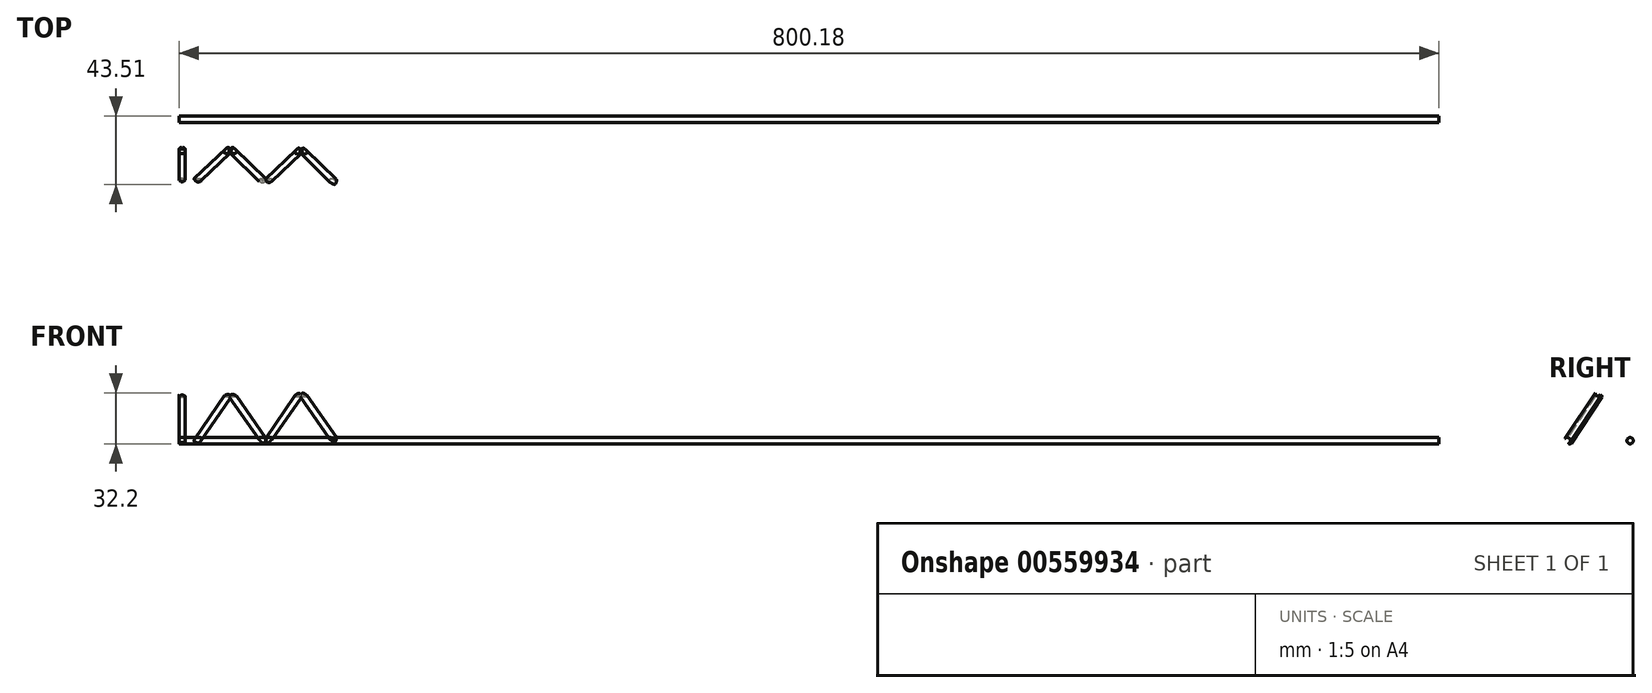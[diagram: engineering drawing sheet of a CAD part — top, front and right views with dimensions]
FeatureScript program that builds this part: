
annotation { "Feature Type Name" : "Feature", "Feature Type Description" : "" }
export const myFeature = defineFeature(function(context is Context, id is Id, definition is map)
    precondition{}
    {
        {
            var Q0;
            Q0=qCreatedBy(makeId("Front.planeOp"),FACE);
            var sketch = newSketch(context, id + "F0", { "sketchPlane" : qUnion([Q0])});
            skLineSegment(sketch, "E0", {"start": v(0, 0) * mm, "end": v(-100, 0) * mm, "construction": true});
            skLineSegment(sketch, "E1", {"start": v(0, 0) * mm, "end": v(700, 0) * mm, "construction": true});
            skLineSegment(sketch, "E2", {"start": v(0, 0) * mm, "end": v(0, 30) * mm, "construction": true});
            skLineSegment(sketch, "E3", {"start": v(0, 30) * mm, "end": v(700, 30) * mm});
            skLineSegment(sketch, "E4", {"start": v(700, 28) * mm, "end": v(700, 30) * mm});
            skLineSegment(sketch, "E5", {"start": v(700, 28) * mm, "end": v(-100, 28) * mm});
            skLineSegment(sketch, "E6", {"start": v(-100, 30) * mm, "end": v(-100, 28) * mm});
            skLineSegment(sketch, "E7", {"start": v(-100, 30) * mm, "end": v(0, 30) * mm});
            skPoint(sketch, "E8", {"position": v(0, 30) * mm});
            skSolve(sketch);
        }
        {
            var Q0;
            Q0=makeQuery(id+"F0.imprint","IMPRINT",FACE,{"disambiguationData":[TD([[makeQuery(id+"F0.imprint","IMPRINT",EDGE,{"derivedFrom":sQuery(id+"F0.wireOp",EDGE,"E3")}),-1.0]])]});
            var Q1;
            Q1=sQuery(id+"F0.wireOp",EDGE,"E7");
            revolve(context, id + "F1", {"surfaceOperationType" : NewSurfaceOperationType.NEW, "entities" : qUnion([Q0]), "axis" : qUnion([Q1]), "revolveType" : RevolveType.FULL});
        }
        {
            var Q0;
            Q0=qCreatedBy(makeId("Right.planeOp"),FACE);
            var sketch = newSketch(context, id + "F2", { "sketchPlane" : qUnion([Q0])});
            skLineSegment(sketch, "E9", {"start": v(0, 0) * mm, "end": v(-20, 0) * mm, "construction": true});
            skLineSegment(sketch, "E10", {"start": v(0, 0) * mm, "end": v(20, 0) * mm, "construction": true});
            skCircle(sketch, "E11", {"center": v(-20, 0) * mm, "radius": 2 * mm});
            skCircle(sketch, "E12", {"center": v(20, 0) * mm, "radius": 2 * mm});
            skSolve(sketch);
        }
        {
            var Q0;
            Q0=makeQuery(id+"F2.imprint","IMPRINT",FACE,{"disambiguationData":[TD([[makeQuery(id+"F2.imprint","IMPRINT",EDGE,{"derivedFrom":sQuery(id+"F2.wireOp",EDGE,"E11")}),1.0]])]});
            var Q1;
            Q1=makeQuery(id+"F2.imprint","IMPRINT",FACE,{"disambiguationData":[TD([[makeQuery(id+"F2.imprint","IMPRINT",EDGE,{"derivedFrom":sQuery(id+"F2.wireOp",EDGE,"E12")}),1.0]])]});
            extrude(context, id + "F3", {"entities" : qUnion([Q0, Q1]), "depth" : 700 * mm, "offsetDistance" : 25 * mm});
        }
        {
            var Q0;
            Q0=makeQuery(id+"F2.imprint","IMPRINT",FACE,{"disambiguationData":[TD([[makeQuery(id+"F2.imprint","IMPRINT",EDGE,{"derivedFrom":sQuery(id+"F2.wireOp",EDGE,"E12")}),1.0]])]});
            var Q1;
            Q1=makeQuery(id+"F2.imprint","IMPRINT",FACE,{"disambiguationData":[TD([[makeQuery(id+"F2.imprint","IMPRINT",EDGE,{"derivedFrom":sQuery(id+"F2.wireOp",EDGE,"E11")}),1.0]])]});
            extrude(context, id + "F4", {"entities" : qUnion([Q0, Q1]), "operationType" : NewBodyOperationType.ADD, "oppositeDirection" : true, "depth" : 100 * mm, "offsetDistance" : 25 * mm});
        }
        {
            var Q0;
            Q0=sQuery(id+"F0.wireOp",VERTEX,"E6.end");
            var Q1;
            Q1=sQuery(id+"F0.wireOp",VERTEX,"E2.end");
            var Q2;
            Q2=sQuery(id+"F2.wireOp",VERTEX,"E9.end");
            cPlane(context, id + "F5", {"entities" : qUnion([Q0, Q1, Q2]), "cplaneType" : CPlaneType.THREE_POINT, "offset" : 25 * mm, "width" : 150 * mm, "height" : 150 * mm});
        }
        {
            var Q0;
            Q0=qCreatedBy(id+"F5.planeOp",FACE);
            var sketch = newSketch(context, id + "F6", { "sketchPlane" : qUnion([Q0])});
            skLineSegment(sketch, "E13", {"start": v(0, 0) * mm, "end": v(0, 24.25) * mm, "construction": true});
            skLineSegment(sketch, "E14", {"start": v(0, 0) * mm, "end": v(0, -11.2) * mm, "construction": true});
            skLineSegment(sketch, "E15", {"start": v(0, 24.25) * mm, "end": v(-100, 24.25) * mm, "construction": true});
            skLineSegment(sketch, "E16", {"start": v(0, -11.2) * mm, "end": v(-100, -11.2) * mm, "construction": true});
            skLineSegment(sketch, "E17", {"start": v(-100, 24.25) * mm, "end": v(-98, 24.25) * mm, "construction": true});
            skLineSegment(sketch, "E18", {"start": v(-100, 24.25) * mm, "end": v(-100, -11.2) * mm});
            skLineSegment(sketch, "E19", {"start": v(-100, 24.25) * mm, "end": v(-98, 24.25) * mm});
            skLineSegment(sketch, "E20", {"start": v(-100, -11.2) * mm, "end": v(-98, -11.2) * mm});
            skLineSegment(sketch, "E21", {"start": v(-98, -11.2) * mm, "end": v(-98, 24.25) * mm});
            skLineSegment(sketch, "E22", {"start": v(0, -11.2) * mm, "end": v(-1, -11.2) * mm, "construction": true});
            skLineSegment(sketch, "E23", {"start": v(-1, -11.2) * mm, "end": v(-21.47, 24.25) * mm});
            skLineSegment(sketch, "E24", {"start": v(-21.47, 24.25) * mm, "end": v(-23.47, 24.25) * mm, "construction": true});
            skLineSegment(sketch, "E25", {"start": v(-23.47, 24.25) * mm, "end": v(-43.94, -11.2) * mm});
            skLineSegment(sketch, "E26", {"start": v(-43.94, -11.2) * mm, "end": v(-45.94, -11.2) * mm});
            skLineSegment(sketch, "E27", {"start": v(-45.94, -11.2) * mm, "end": v(-66.42, 24.25) * mm});
            skLineSegment(sketch, "E28", {"start": v(-66.42, 24.25) * mm, "end": v(-68.42, 24.25) * mm, "construction": true});
            skLineSegment(sketch, "E29", {"start": v(-68.42, 24.25) * mm, "end": v(-88.89, -11.2) * mm});
            skLineSegment(sketch, "E30", {"start": v(-68.42, 24.25) * mm, "end": v(-70.15, 25.25) * mm});
            skLineSegment(sketch, "E31", {"start": v(-88.89, -11.2) * mm, "end": v(-90.62, -10.2) * mm});
            skLineSegment(sketch, "E32", {"start": v(-90.62, -10.2) * mm, "end": v(-70.15, 25.25) * mm});
            skLineSegment(sketch, "E33", {"start": v(-66.42, 24.25) * mm, "end": v(-64.68, 25.25) * mm});
            skLineSegment(sketch, "E34", {"start": v(-45.94, -11.2) * mm, "end": v(-44.21, -10.2) * mm});
            skLineSegment(sketch, "E35", {"start": v(-64.68, 25.25) * mm, "end": v(-44.21, -10.2) * mm});
            skLineSegment(sketch, "E36", {"start": v(-45.43, -10.2) * mm, "end": v(-43.94, -11.2) * mm});
            skLineSegment(sketch, "E37", {"start": v(-23.47, 24.25) * mm, "end": v(-25.2, 25.25) * mm});
            skLineSegment(sketch, "E38", {"start": v(-25.2, 25.25) * mm, "end": v(-45.43, -10.2) * mm});
            skLineSegment(sketch, "E39", {"start": v(-21.47, 24.25) * mm, "end": v(-19.74, 25.25) * mm});
            skLineSegment(sketch, "E40", {"start": v(-1, -11.2) * mm, "end": v(0.73, -10.2) * mm});
            skLineSegment(sketch, "E41", {"start": v(0.73, -10.2) * mm, "end": v(-19.74, 25.25) * mm});
            skSolve(sketch);
        }
        {
            var Q0;
            Q0=makeQuery(id+"F6.imprint","IMPRINT",FACE,{"disambiguationData":[TD([[makeQuery(id+"F6.imprint","IMPRINT",EDGE,{"derivedFrom":sQuery(id+"F6.wireOp",EDGE,"E18")}),1.0]])]});
            var Q1;
            Q1=sQuery(id+"F6.wireOp",EDGE,"E21");
            revolve(context, id + "F7", {"surfaceOperationType" : NewSurfaceOperationType.NEW, "entities" : qUnion([Q0]), "axis" : qUnion([Q1]), "revolveType" : RevolveType.FULL});
        }
        {
            var Q0;
            Q0=makeQuery(id+"F6.imprint","IMPRINT",FACE,{"disambiguationData":[TD([[makeQuery(id+"F6.imprint","IMPRINT",EDGE,{"derivedFrom":sQuery(id+"F6.wireOp",EDGE,"E29")}),-1.0]])]});
            var Q1;
            Q1=sQuery(id+"F6.wireOp",EDGE,"E29");
            revolve(context, id + "F8", {"surfaceOperationType" : NewSurfaceOperationType.NEW, "entities" : qUnion([Q0]), "axis" : qUnion([Q1]), "revolveType" : RevolveType.FULL});
        }
        {
            var Q0;
            {var subQ5=sQuery(id+"F6.wireOp",EDGE,"E27");Q0=makeQuery(id+"F6.imprint","IMPRINT",FACE,{"disambiguationData":[TD([[makeQuery(id+"F6.imprint","IMPRINT",EDGE,{"derivedFrom":subQ5}),-1.0]])]});}
            var Q1;
            {var subQ0=sQuery(id+"F6.wireOp",EDGE,"E35");var subQ1=sQuery(id+"F6.wireOp",EDGE,"E34");var subQ2=makeQuery(id+"F6.imprint","INTERSECT",VERTEX,{"derivedFrom":[subQ1,subQ0]});Q1=makeQuery(id+"F6.imprint","IMPRINT",FACE,{"disambiguationData":[TD([[makeQuery(id+"F6.imprint","IMPRINT",EDGE,{"disambiguationData":[TD([[subQ2,1.0]])],"derivedFrom":subQ1}),1.0]])]});}
            var Q2;
            Q2=sQuery(id+"F6.wireOp",EDGE,"E27");
            revolve(context, id + "F9", {"surfaceOperationType" : NewSurfaceOperationType.NEW, "entities" : qUnion([Q0, Q1]), "axis" : qUnion([Q2]), "revolveType" : RevolveType.FULL});
        }
        {
            var Q0;
            {var subQ1=sQuery(id+"F6.wireOp",EDGE,"E25");Q0=makeQuery(id+"F6.imprint","IMPRINT",FACE,{"disambiguationData":[TD([[makeQuery(id+"F6.imprint","IMPRINT",EDGE,{"derivedFrom":subQ1}),-1.0]])]});}
            var Q1;
            {var subQ0=sQuery(id+"F6.wireOp",EDGE,"E35");var subQ1=sQuery(id+"F6.wireOp",EDGE,"E34");var subQ2=makeQuery(id+"F6.imprint","INTERSECT",VERTEX,{"derivedFrom":[subQ1,subQ0]});Q1=makeQuery(id+"F6.imprint","IMPRINT",FACE,{"disambiguationData":[TD([[makeQuery(id+"F6.imprint","IMPRINT",EDGE,{"disambiguationData":[TD([[subQ2,1.0]])],"derivedFrom":subQ1}),1.0]])]});}
            var Q2;
            Q2=sQuery(id+"F6.wireOp",EDGE,"E25");
            revolve(context, id + "F10", {"surfaceOperationType" : NewSurfaceOperationType.NEW, "entities" : qUnion([Q0, Q1]), "axis" : qUnion([Q2]), "revolveType" : RevolveType.FULL});
        }
        {
            var Q0;
            Q0=makeQuery(id+"F6.imprint","IMPRINT",FACE,{"disambiguationData":[TD([[makeQuery(id+"F6.imprint","IMPRINT",EDGE,{"derivedFrom":sQuery(id+"F6.wireOp",EDGE,"E23")}),-1.0]])]});
            var Q1;
            Q1=sQuery(id+"F6.wireOp",EDGE,"E23");
            revolve(context, id + "F11", {"surfaceOperationType" : NewSurfaceOperationType.NEW, "entities" : qUnion([Q0]), "axis" : qUnion([Q1]), "revolveType" : RevolveType.FULL});
        }
        {
            var Q0;
            Q0=makeQuery(id+"F0.imprint","IMPRINT",FACE,{"disambiguationData":[TD([[makeQuery(id+"F0.imprint","IMPRINT",EDGE,{"derivedFrom":sQuery(id+"F0.wireOp",EDGE,"E3")}),-1.0]])]});
            var Q1;
            Q1=sQuery(id+"F0.wireOp",EDGE,"E7");
            revolve(context, id + "F12", {"operationType" : NewBodyOperationType.REMOVE, "surfaceOperationType" : NewSurfaceOperationType.NEW, "entities" : qUnion([Q0]), "axis" : qUnion([Q1]), "revolveType" : RevolveType.FULL, "oppositeDirection" : true});
        }
        {
            var Q0;
            Q0=makeQuery(id+"F2.imprint","IMPRINT",FACE,{"disambiguationData":[TD([[makeQuery(id+"F2.imprint","IMPRINT",EDGE,{"derivedFrom":sQuery(id+"F2.wireOp",EDGE,"E11")}),1.0]])]});
            extrude(context, id + "F13", {"entities" : qUnion([Q0]), "operationType" : NewBodyOperationType.REMOVE, "endBound" : BoundingType.SYMMETRIC, "depth" : 2000 * mm, "offsetDistance" : 25 * mm});
        }
    });
